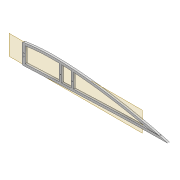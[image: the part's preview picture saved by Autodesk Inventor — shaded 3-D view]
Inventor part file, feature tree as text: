
AUTODESK INVENTOR PART (.ipt)
format: ipt  version: 2022 (Build 260153000, 153)  size: 356,352 bytes
history: native  units: mm
features: extrude x7, sketch x7, projected_geometry x5, shell x1, fillet x1, plane x1
ambient origin geometry x8: Origin, YZ Plane, XZ Plane, XY Plane, X Axis, Y Axis, Z Axis, Center Point
bodies: Solid1 (feature_tree)
feature tree (22):
  extrude  "Extrusion1"  Depth=5.0mm
  shell  "Shell1"  Thickness=2.0mm
  extrude  "Extrusion8"  Depth=5.9mm
  extrude  "Extrusion3"  Depth=10.0mm TaperAngle=0.0deg
  extrude  "Extrusion4"  Depth=2.0mm
  fillet  "Fillet1"  Radius=5.0mm
  extrude  "Extrusion5"  Depth=2.5mm
  plane  "Work Plane2"
  extrude  "Extrusion9"  Depth=1.6mm
  extrude  "Extrusion10"  Depth=0.5mm
  sketch  "Sketch3"  dims[d0=4.0mm d1=0.0mm d2=5.0mm d7=2.0mm]
  sketch  "Sketch8"  dims[d8=2.0mm d9=5.9mm]
  sketch  "Sketch9"  dims[d13=10.0mm d14=0.0mm d16=10.0mm d17=0.0mm]
  sketch  "Sketch10"  dims[d22=4.0mm d23=0.0mm d31=2.0mm d32=5.0mm]
  projected_geometry  "Projected Loop4"
  projected_geometry  "Projected Loop10"
  sketch  "Sketch24"  dims[d34=1.6mm d35=2.5mm]
  projected_geometry  "Projected Loop11"
  projected_geometry  "Projected Loop12"
  sketch  "Sketch26"  dims[d37=5.0mm d38=1.6mm]
  projected_geometry  "Projected Loop13"
  sketch  "Sketch27"  dims[d40=2.5mm d62=67.0mm d63=6.0mm d64=4.0mm d65=0.0mm d66=3.0mm d67=12.0mm d68=75.0mm d69=20.0mm d70=0.5mm d71=10.0mm d72=0.0mm d73=10.0mm d74=0.0mm]
